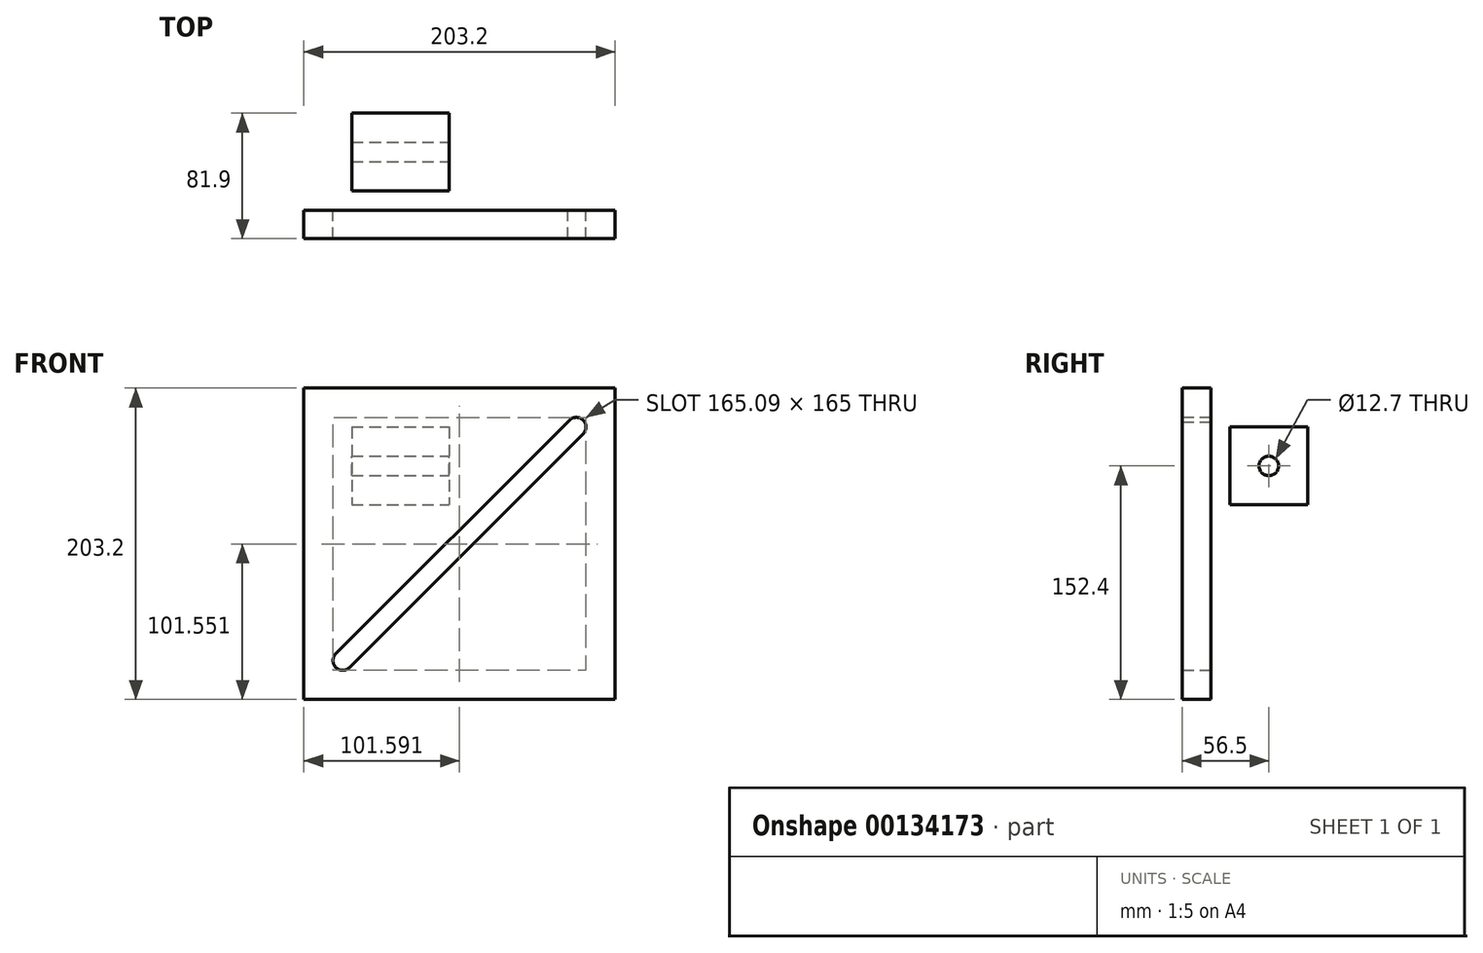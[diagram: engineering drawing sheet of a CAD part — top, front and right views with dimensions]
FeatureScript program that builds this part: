
annotation { "Feature Type Name" : "Feature", "Feature Type Description" : "" }
export const myFeature = defineFeature(function(context is Context, id is Id, definition is map)
    precondition{}
    {
        {
            var Q0;
            Q0=qCreatedBy(makeId("Front.planeOp"),FACE);
            var sketch = newSketch(context, id + "F0", { "sketchPlane" : qUnion([Q0])});
            skLineSegment(sketch, "E0.bottom", {"start": v(108.45, -101.6) * mm, "end": v(-94.75, -101.6) * mm});
            skLineSegment(sketch, "E0.top", {"start": v(108.45, 101.6) * mm, "end": v(-94.75, 101.6) * mm});
            skLineSegment(sketch, "E0.left", {"start": v(108.45, -101.6) * mm, "end": v(108.45, 101.6) * mm});
            skLineSegment(sketch, "E0.right", {"start": v(-94.75, -101.6) * mm, "end": v(-94.75, 101.6) * mm});
            skPoint(sketch, "E0.middle", {"position": v(6.85, 0) * mm});
            skArc(sketch, "E1", {"start": v(-73.84, -71.7) * mm, "mid": v(-73.85, -80.69) * mm, "end": v(-64.86, -80.7) * mm});
            skArc(sketch, "E2", {"start": v(87.54, 71.7) * mm, "mid": v(86.98, 81.19) * mm, "end": v(77.63, 79.52) * mm});
            skLineSegment(sketch, "E3", {"start": v(77.63, 79.52) * mm, "end": v(-73.84, -71.7) * mm});
            skLineSegment(sketch, "E4", {"start": v(-64.86, -80.7) * mm, "end": v(87.54, 71.7) * mm});
            skSolve(sketch);
        }
        {
            var Q0;
            Q0 = qSketchRegion(id + "F0", true);
            extrude(context, id + "F1", {"entities" : qUnion([Q0]), "depth" : 18.64 * mm});
        }
        {
            var Q0;
            Q0=qCreatedBy(makeId("Right.planeOp"),FACE);
            var sketch = newSketch(context, id + "F2", { "sketchPlane" : qUnion([Q0])});
            skLineSegment(sketch, "E5.bottom", {"start": v(12.46, 76.2) * mm, "end": v(63.26, 76.2) * mm});
            skLineSegment(sketch, "E5.top", {"start": v(12.46, 25.4) * mm, "end": v(63.26, 25.4) * mm});
            skLineSegment(sketch, "E5.left", {"start": v(12.46, 76.2) * mm, "end": v(12.46, 25.4) * mm});
            skLineSegment(sketch, "E5.right", {"start": v(63.26, 76.2) * mm, "end": v(63.26, 25.4) * mm});
            skSolve(sketch);
        }
        {
            var Q0;
            Q0 = qSketchRegion(id + "F2", true);
            extrude(context, id + "F3", {"entities" : qUnion([Q0]), "oppositeDirection" : true, "depth" : 63.5 * mm});
        }
        {
            var Q0;
            Q0=makeQuery(id+"F2.imprint","IMPRINT",FACE,{"disambiguationData":[TD([[makeQuery(id+"F2.imprint","IMPRINT",EDGE,{"derivedFrom":sQuery(id+"F2.wireOp",EDGE,"E5.bottom")}),-1.0]])]});
            var sketch = newSketch(context, id + "F5", { "sketchPlane" : qUnion([Q0])});
            skCircle(sketch, "E6", {"center": v(37.86, 50.8) * mm, "radius": 6.35 * mm});
            skSolve(sketch);
        }
        {
            var Q0;
            Q0=makeQuery(id+"F5.imprint","IMPRINT",FACE,{"disambiguationData":[TD([[makeQuery(id+"F5.imprint","IMPRINT",EDGE,{"derivedFrom":sQuery(id+"F5.wireOp",EDGE,"E6")}),1.0]])]});
            extrude(context, id + "F4", {"entities" : qUnion([Q0]), "operationType" : NewBodyOperationType.REMOVE, "endBound" : BoundingType.THROUGH_ALL, "oppositeDirection" : true, "depth" : 25.4 * mm});
        }
    });
